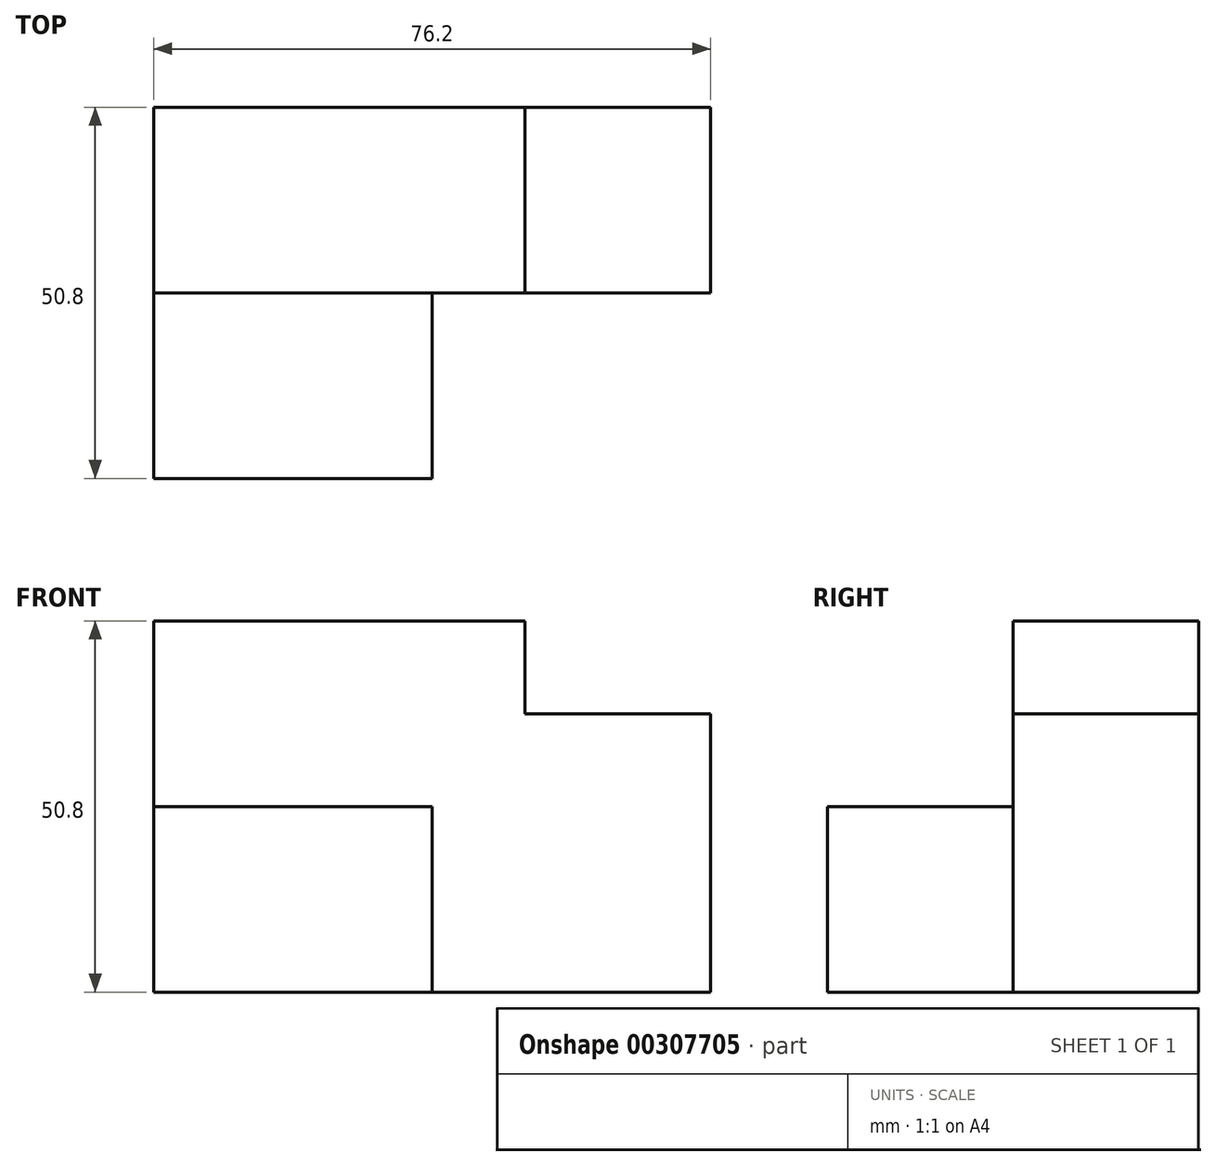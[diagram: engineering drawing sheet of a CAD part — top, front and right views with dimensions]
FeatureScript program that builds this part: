
annotation { "Feature Type Name" : "Feature", "Feature Type Description" : "" }
export const myFeature = defineFeature(function(context is Context, id is Id, definition is map)
    precondition{}
    {
        {
            var Q0;
            Q0=qCreatedBy(makeId("Top.planeOp"),FACE);
            var sketch = newSketch(context, id + "F0", { "sketchPlane" : qUnion([Q0])});
            skLineSegment(sketch, "E0.bottom", {"start": v(-36.65, 25.55) * mm, "end": v(39.55, 25.55) * mm});
            skLineSegment(sketch, "E0.top", {"start": v(-36.65, 0.15) * mm, "end": v(39.55, 0.15) * mm});
            skLineSegment(sketch, "E0.left", {"start": v(-36.65, 25.55) * mm, "end": v(-36.65, 0.15) * mm});
            skLineSegment(sketch, "E0.right", {"start": v(39.55, 25.55) * mm, "end": v(39.55, 0.15) * mm});
            skSolve(sketch);
        }
        {
            var Q0;
            Q0=makeQuery(id+"F0.imprint","IMPRINT",FACE,{"disambiguationData":[TD([[makeQuery(id+"F0.imprint","IMPRINT",EDGE,{"derivedFrom":sQuery(id+"F0.wireOp",EDGE,"E0.bottom")}),-1.0]])]});
            extrude(context, id + "F1", {"entities" : qUnion([Q0]), "depth" : 38.1 * mm});
        }
        {
            var Q0;
            Q0=makeQuery(id+"F1.opExtrude","SWEPT_FACE",FACE,{"disambiguationData":[OSD([sQuery(id+"F0.wireOp",EDGE,"E0.top")])]});
            var sketch = newSketch(context, id + "F2", { "sketchPlane" : qUnion([Q0])});
            skLineSegment(sketch, "E1.bottom", {"start": v(-36.65, 0) * mm, "end": v(1.45, 0) * mm});
            skLineSegment(sketch, "E1.top", {"start": v(-36.65, 25.4) * mm, "end": v(1.45, 25.4) * mm});
            skLineSegment(sketch, "E1.left", {"start": v(-36.65, 0) * mm, "end": v(-36.65, 25.4) * mm});
            skLineSegment(sketch, "E1.right", {"start": v(1.45, 0) * mm, "end": v(1.45, 25.4) * mm});
            skSolve(sketch);
        }
        {
            var Q0;
            Q0=makeQuery(id+"F2.imprint","IMPRINT",FACE,{"disambiguationData":[TD([[makeQuery(id+"F2.imprint","IMPRINT",EDGE,{"derivedFrom":sQuery(id+"F2.wireOp",EDGE,"E1.bottom")}),1.0]])]});
            extrude(context, id + "F3", {"entities" : qUnion([Q0]), "operationType" : NewBodyOperationType.ADD, "depth" : 25.4 * mm});
        }
        {
            var Q0;
            Q0=makeQuery(id+"F1.opExtrude","CAP_FACE",FACE,{"disambiguationData":[OSD([sQuery(id+"F0.wireOp",EDGE,"E0.bottom"),sQuery(id+"F0.wireOp",EDGE,"E0.top"),sQuery(id+"F0.wireOp",EDGE,"E0.left"),sQuery(id+"F0.wireOp",EDGE,"E0.right")])],"isStart":false});
            var sketch = newSketch(context, id + "F4", { "sketchPlane" : qUnion([Q0])});
            skLineSegment(sketch, "E2.bottom", {"start": v(-36.65, 25.55) * mm, "end": v(14.15, 25.55) * mm});
            skLineSegment(sketch, "E2.top", {"start": v(-36.65, 0.15) * mm, "end": v(14.15, 0.15) * mm});
            skLineSegment(sketch, "E2.left", {"start": v(-36.65, 25.55) * mm, "end": v(-36.65, 0.15) * mm});
            skLineSegment(sketch, "E2.right", {"start": v(14.15, 25.55) * mm, "end": v(14.15, 0.15) * mm});
            skSolve(sketch);
        }
        {
            var Q0;
            Q0=makeQuery(id+"F4.imprint","IMPRINT",FACE,{"disambiguationData":[TD([[makeQuery(id+"F4.imprint","IMPRINT",EDGE,{"derivedFrom":sQuery(id+"F4.wireOp",EDGE,"E2.bottom")}),-1.0]])]});
            extrude(context, id + "F5", {"entities" : qUnion([Q0]), "operationType" : NewBodyOperationType.ADD, "depth" : 12.7 * mm});
        }
    });
